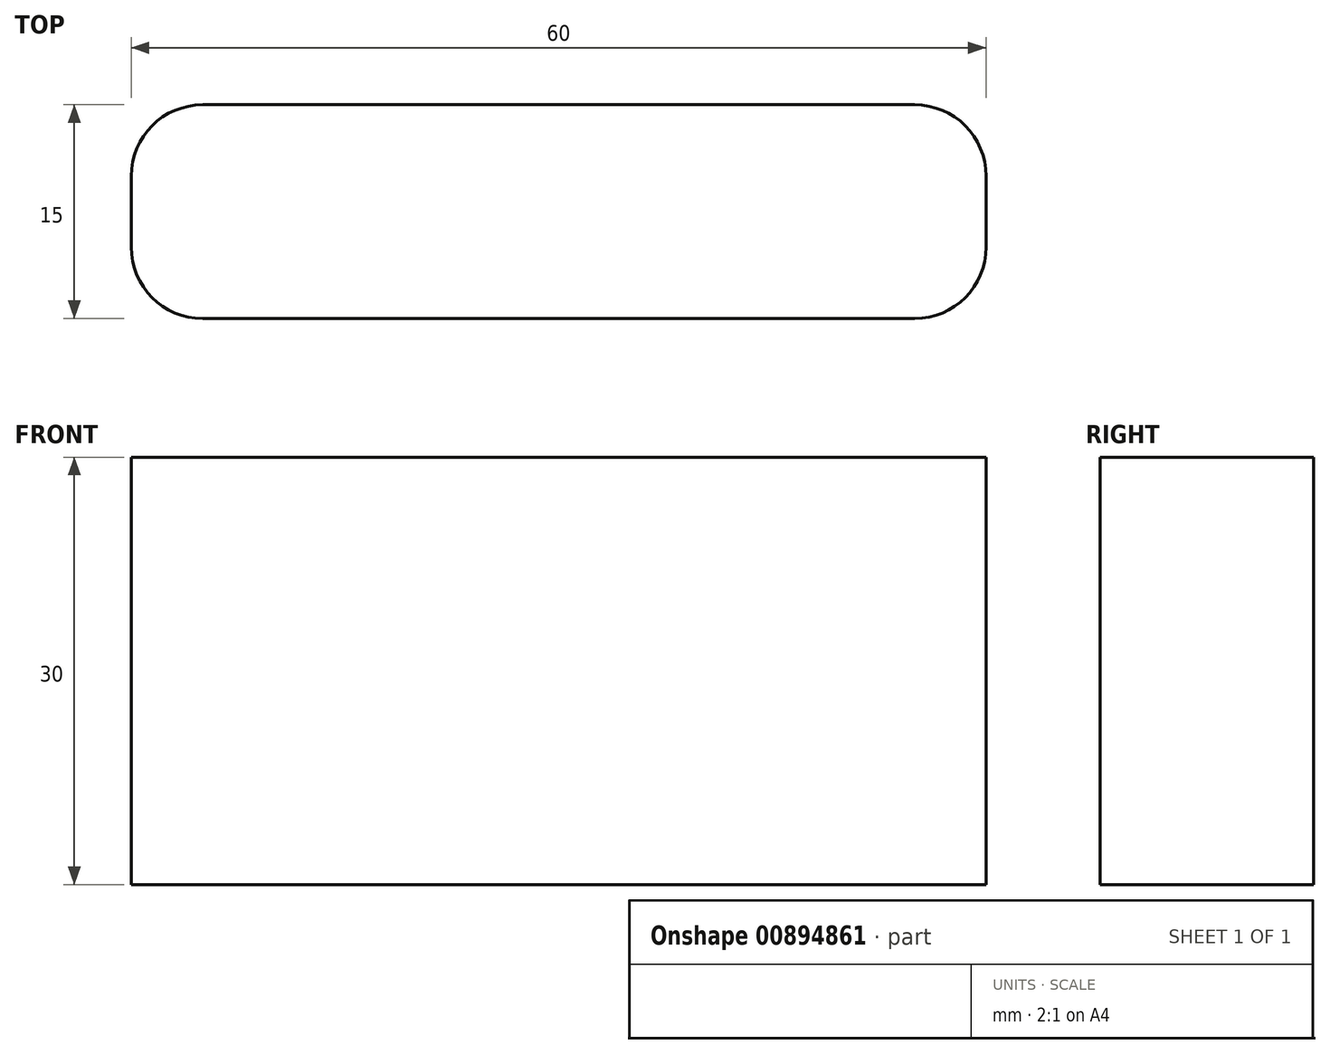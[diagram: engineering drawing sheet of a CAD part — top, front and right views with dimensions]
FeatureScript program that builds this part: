
annotation { "Feature Type Name" : "Feature", "Feature Type Description" : "" }
export const myFeature = defineFeature(function(context is Context, id is Id, definition is map)
    precondition{}
    {
        {
            var Q0;
            Q0=qCreatedBy(makeId("Top.planeOp"),FACE);
            var sketch = newSketch(context, id + "F0", { "sketchPlane" : qUnion([Q0])});
            skLineSegment(sketch, "E0", {"start": v(0, -5.81) * mm, "end": v(0, -10.81) * mm});
            skLineSegment(sketch, "E1", {"start": v(-5, -15.81) * mm, "end": v(-55, -15.81) * mm});
            skLineSegment(sketch, "E2", {"start": v(-60, -10.81) * mm, "end": v(-60, -5.81) * mm});
            skLineSegment(sketch, "E3", {"start": v(-5, -0.81) * mm, "end": v(-55, -0.81) * mm});
            skPoint(sketch, "E4.visualSharp", {"position": v(-60, -0.81) * mm});
            skArc(sketch, "E4.filletArc", {"start": v(-55, -0.81) * mm, "mid": v(-58.54, -2.28) * mm, "end": v(-60, -5.81) * mm});
            skPoint(sketch, "E5.visualSharp", {"position": v(-60, -15.81) * mm});
            skArc(sketch, "E5.filletArc", {"start": v(-60, -10.81) * mm, "mid": v(-58.54, -14.35) * mm, "end": v(-55, -15.81) * mm});
            skPoint(sketch, "E6.visualSharp", {"position": v(0, -15.81) * mm});
            skArc(sketch, "E6.filletArc", {"start": v(-5, -15.81) * mm, "mid": v(-1.46, -14.35) * mm, "end": v(0, -10.81) * mm});
            skPoint(sketch, "E7.visualSharp", {"position": v(0, -0.81) * mm});
            skArc(sketch, "E7.filletArc", {"start": v(0, -5.81) * mm, "mid": v(-1.46, -2.28) * mm, "end": v(-5, -0.81) * mm});
            skSolve(sketch);
        }
        {
            var Q0;
            Q0=makeQuery(id+"F0.imprint","IMPRINT",FACE,{"disambiguationData":[TD([[makeQuery(id+"F0.imprint","IMPRINT",EDGE,{"derivedFrom":sQuery(id+"F0.wireOp",EDGE,"QmRtS9SP-vnO7-7tmh-7Oug-WLXFY4kIVe7P")}),-1.0]])]});
            var Q1;
            Q1=makeQuery(id+"F0.imprint","IMPRINT",FACE,{"disambiguationData":[TD([[makeQuery(id+"F0.imprint","IMPRINT",EDGE,{"derivedFrom":sQuery(id+"F0.wireOp",EDGE,"E0")}),-1.0]])]});
            extrude(context, id + "F1", {"entities" : qUnion([Q0, Q1]), "depth" : 30 * mm, "offsetDistance" : 25 * mm});
        }
    });
